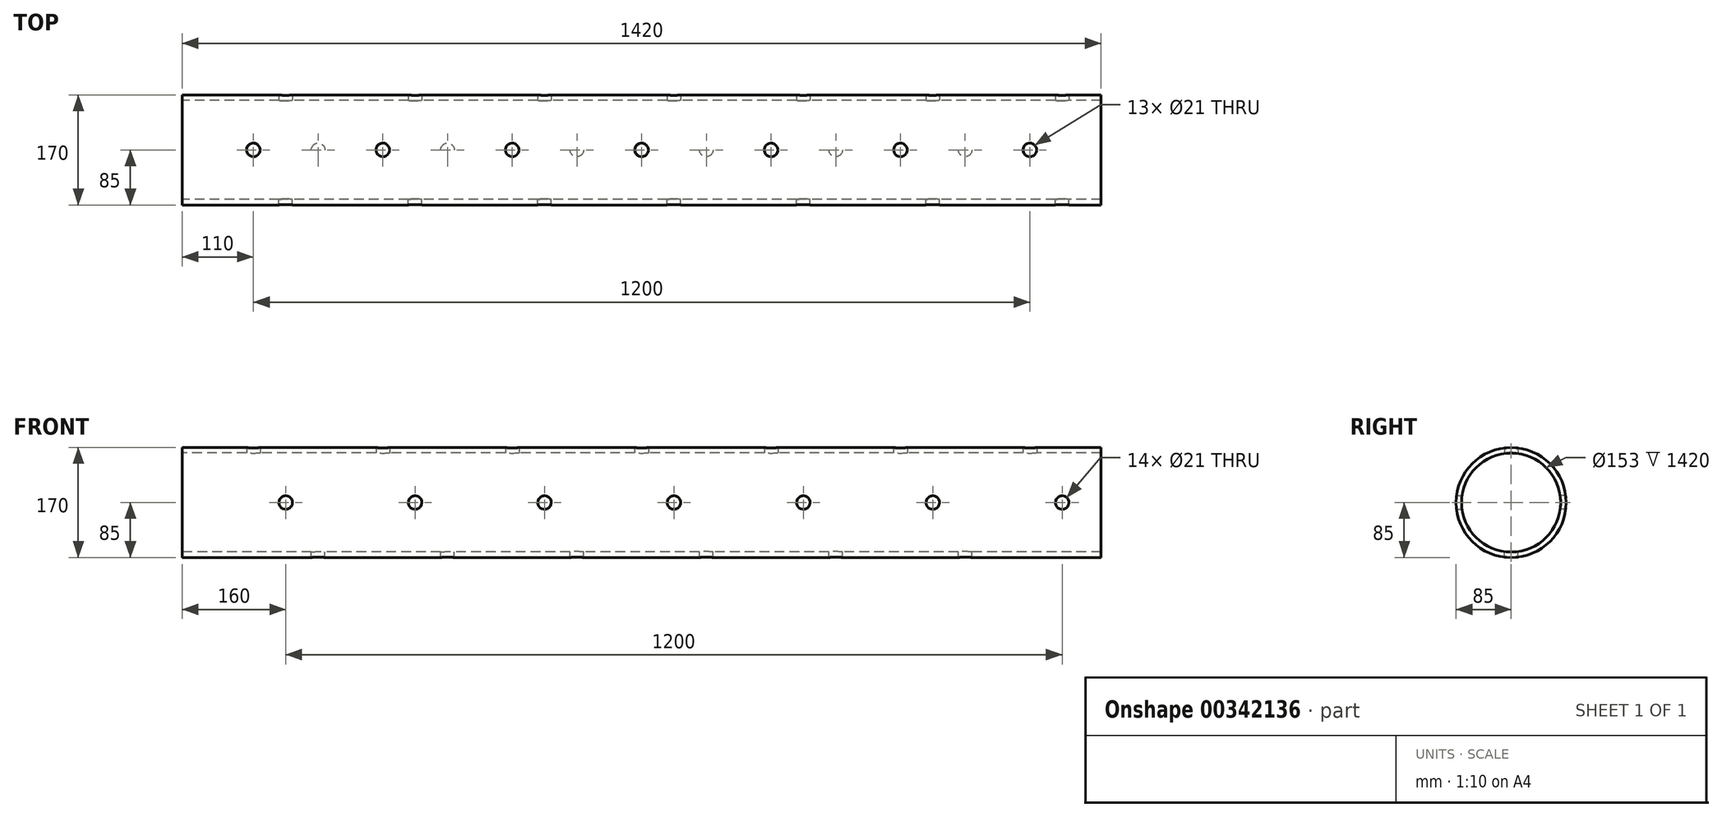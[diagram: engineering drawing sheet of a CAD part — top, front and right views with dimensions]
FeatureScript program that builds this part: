
annotation { "Feature Type Name" : "Feature", "Feature Type Description" : "" }
export const myFeature = defineFeature(function(context is Context, id is Id, definition is map)
    precondition{}
    {
        {
            var Q0;
            Q0=qCreatedBy(makeId("Right.planeOp"),FACE);
            var sketch = newSketch(context, id + "F0", { "sketchPlane" : qUnion([Q0])});
            skCircle(sketch, "E0", {"center": v(0, 0) * mm, "radius": 85 * mm});
            skCircle(sketch, "E1", {"center": v(0, 0) * mm, "radius": 76.5 * mm});
            skSolve(sketch);
        }
        {
            var Q0;
            Q0=makeQuery(id+"F0.imprint","IMPRINT",FACE,{"disambiguationData":[TD([[makeQuery(id+"F0.imprint","IMPRINT",EDGE,{"derivedFrom":sQuery(id+"F0.wireOp",EDGE,"E0")}),1.0]])]});
            extrude(context, id + "F1", {"entities" : qUnion([Q0]), "depth" : 1420 * mm});
        }
        {
            var Q0;
            Q0=qCreatedBy(makeId("Front.planeOp"),FACE);
            var sketch = newSketch(context, id + "F2", { "sketchPlane" : qUnion([Q0])});
            skLineSegment(sketch, "E2", {"start": v(0, 85) * mm, "end": v(1420, 85) * mm});
            skLineSegment(sketch, "E3", {"start": v(1420, -85) * mm, "end": v(0, -85) * mm});
            skLineSegment(sketch, "E4.0", {"start": v(0, 85) * mm, "end": v(0, -85) * mm});
            skLineSegment(sketch, "E5.0", {"start": v(1420, 85) * mm, "end": v(1420, -85) * mm});
            skLineSegment(sketch, "E6", {"start": v(0, 0) * mm, "end": v(160, 0) * mm});
            skLineSegment(sketch, "E7", {"start": v(160, 0) * mm, "end": v(360, 0) * mm});
            skLineSegment(sketch, "E8", {"start": v(360, 0) * mm, "end": v(560, 0) * mm});
            skLineSegment(sketch, "E9", {"start": v(560, 0) * mm, "end": v(760, 0) * mm});
            skLineSegment(sketch, "E10", {"start": v(760, 0) * mm, "end": v(960, 0) * mm});
            skLineSegment(sketch, "E11", {"start": v(960, 0) * mm, "end": v(1160, 0) * mm});
            skLineSegment(sketch, "E12", {"start": v(1160, 0) * mm, "end": v(1360, 0) * mm});
            skCircle(sketch, "E13", {"center": v(160, 0) * mm, "radius": 10.5 * mm});
            skCircle(sketch, "E14", {"center": v(360, 0) * mm, "radius": 10.5 * mm});
            skCircle(sketch, "E15", {"center": v(560, 0) * mm, "radius": 10.5 * mm});
            skCircle(sketch, "E16", {"center": v(760, 0) * mm, "radius": 10.5 * mm});
            skCircle(sketch, "E17", {"center": v(960, 0) * mm, "radius": 10.5 * mm});
            skCircle(sketch, "E18", {"center": v(1160, 0) * mm, "radius": 10.5 * mm});
            skCircle(sketch, "E19", {"center": v(1360, 0) * mm, "radius": 10.5 * mm});
            skSolve(sketch);
        }
        {
            var Q0;
            Q0=sQuery(id+"F2.wireOp",VERTEX,"E7.start");
            var Q1;
            Q1=sQuery(id+"F2.wireOp",VERTEX,"E8.start");
            var Q2;
            Q2=sQuery(id+"F2.wireOp",VERTEX,"E9.start");
            var Q3;
            Q3=sQuery(id+"F2.wireOp",VERTEX,"E16.center");
            var Q4;
            Q4=sQuery(id+"F2.wireOp",VERTEX,"E11.start");
            var Q5;
            Q5=sQuery(id+"F2.wireOp",VERTEX,"E12.end");
            var Q6;
            Q6=sQuery(id+"F2.wireOp",VERTEX,"E18.center");
            var Q7;
            Q7=makeQuery(id+"F1.opExtrude","SWEPT_BODY",BODY,{"disambiguationData":[OSD([sQuery(id+"F0.wireOp",EDGE,"E0"),sQuery(id+"F0.wireOp",EDGE,"E1")])]});
            hole(context, id + "F3", {"style" : HoleStyle.SIMPLE, "endStyle" : HoleEndStyle.BLIND, "holeDiameter" : 21 * mm, "holeDepth" : 1000 * mm, "tappedDepth" : 12 * mm, "tapClearance" : 3, "locations" : qUnion([Q0, Q1, Q2, Q3, Q4, Q5, Q6]), "scope" : qUnion([Q7])});
        }
        {
            var Q0;
            Q0=qCreatedBy(makeId("Front.planeOp"),FACE);
            var sketch = newSketch(context, id + "F4", { "sketchPlane" : qUnion([Q0])});
            skLineSegment(sketch, "E20.0", {"start": v(0, 85) * mm, "end": v(0, -85) * mm});
            skLineSegment(sketch, "E21", {"start": v(0, 85) * mm, "end": v(1420, 85) * mm});
            skLineSegment(sketch, "E22", {"start": v(1420, -85) * mm, "end": v(0, -85) * mm});
            skLineSegment(sketch, "E23.0", {"start": v(1420, 85) * mm, "end": v(1420, -85) * mm});
            skLineSegment(sketch, "E24", {"start": v(0, 0) * mm, "end": v(160, 0) * mm});
            skLineSegment(sketch, "E25", {"start": v(160, 0) * mm, "end": v(360, 0) * mm});
            skLineSegment(sketch, "E26", {"start": v(360, 0) * mm, "end": v(560, 0) * mm});
            skLineSegment(sketch, "E27", {"start": v(560, 0) * mm, "end": v(760, 0) * mm});
            skLineSegment(sketch, "E28", {"start": v(760, 0) * mm, "end": v(960, 0) * mm});
            skLineSegment(sketch, "E29", {"start": v(960, 0) * mm, "end": v(1160, 0) * mm});
            skLineSegment(sketch, "E30", {"start": v(1160, 0) * mm, "end": v(1360, 0) * mm});
            skSolve(sketch);
        }
        {
            var Q0;
            Q0=sQuery(id+"F4.wireOp",VERTEX,"E25.start");
            var Q1;
            Q1=sQuery(id+"F4.wireOp",VERTEX,"E26.start");
            var Q2;
            Q2=sQuery(id+"F4.wireOp",VERTEX,"E27.start");
            var Q3;
            Q3=sQuery(id+"F4.wireOp",VERTEX,"E28.start");
            var Q4;
            Q4=sQuery(id+"F4.wireOp",VERTEX,"E28.end");
            var Q5;
            Q5=sQuery(id+"F4.wireOp",VERTEX,"E29.end");
            var Q6;
            Q6=sQuery(id+"F4.wireOp",VERTEX,"E30.end");
            var Q7;
            Q7=makeQuery(id+"F1.opExtrude","SWEPT_BODY",BODY,{"disambiguationData":[OSD([sQuery(id+"F0.wireOp",EDGE,"E0"),sQuery(id+"F0.wireOp",EDGE,"E1")])]});
            hole(context, id + "F5", {"style" : HoleStyle.SIMPLE, "endStyle" : HoleEndStyle.BLIND, "oppositeDirection" : true, "holeDiameter" : 21 * mm, "holeDepth" : 1000 * mm, "tappedDepth" : 12 * mm, "tapClearance" : 3, "locations" : qUnion([Q0, Q1, Q2, Q3, Q4, Q5, Q6]), "scope" : qUnion([Q7])});
        }
        {
            var Q0;
            Q0=qCreatedBy(makeId("Top.planeOp"),FACE);
            var sketch = newSketch(context, id + "F6", { "sketchPlane" : qUnion([Q0])});
            skLineSegment(sketch, "E31", {"start": v(0, 85) * mm, "end": v(1420, 85) * mm});
            skLineSegment(sketch, "E32.0", {"start": v(0, 85) * mm, "end": v(0, -85) * mm});
            skLineSegment(sketch, "E33", {"start": v(1420, -85) * mm, "end": v(0, -85) * mm});
            skLineSegment(sketch, "E34.0", {"start": v(1420, 85) * mm, "end": v(1420, -85) * mm});
            skLineSegment(sketch, "E35", {"start": v(0, 0) * mm, "end": v(110, 0) * mm});
            skLineSegment(sketch, "E36", {"start": v(110, 0) * mm, "end": v(310, 0) * mm});
            skLineSegment(sketch, "E37", {"start": v(310, 0) * mm, "end": v(510, 0) * mm});
            skLineSegment(sketch, "E38", {"start": v(510, 0) * mm, "end": v(710, 0) * mm});
            skLineSegment(sketch, "E39", {"start": v(710, 0) * mm, "end": v(910, 0) * mm});
            skLineSegment(sketch, "E40", {"start": v(910, 0) * mm, "end": v(1110, 0) * mm});
            skLineSegment(sketch, "E41", {"start": v(1110, 0) * mm, "end": v(1310, 0) * mm});
            skLineSegment(sketch, "E42", {"start": v(0, 0) * mm, "end": v(-55.2, 0) * mm});
            skLineSegment(sketch, "E43", {"start": v(-55.2, 0) * mm, "end": v(1452.61, 0) * mm});
            skPoint(sketch, "E44", {"position": v(110, 0) * mm});
            skPoint(sketch, "E45", {"position": v(310, 0) * mm});
            skPoint(sketch, "E46", {"position": v(510, 0) * mm});
            skPoint(sketch, "E47", {"position": v(710, 0) * mm});
            skPoint(sketch, "E48", {"position": v(910, 0) * mm});
            skPoint(sketch, "E49", {"position": v(1110, 0) * mm});
            skPoint(sketch, "E50", {"position": v(1310, 0) * mm});
            skSolve(sketch);
        }
        {
            var Q0;
            Q0=sQuery(id+"F6.wireOp",VERTEX,"E46");
            var Q1;
            Q1=sQuery(id+"F6.wireOp",VERTEX,"E45");
            var Q2;
            Q2=sQuery(id+"F6.wireOp",VERTEX,"E44");
            var Q3;
            Q3=sQuery(id+"F6.wireOp",VERTEX,"E48");
            var Q4;
            Q4=sQuery(id+"F6.wireOp",VERTEX,"E47");
            var Q5;
            Q5=sQuery(id+"F6.wireOp",VERTEX,"E49");
            var Q6;
            Q6=sQuery(id+"F6.wireOp",VERTEX,"E50");
            var Q7;
            Q7=makeQuery(id+"F1.opExtrude","SWEPT_BODY",BODY,{"disambiguationData":[OSD([sQuery(id+"F0.wireOp",EDGE,"E0"),sQuery(id+"F0.wireOp",EDGE,"E1")])]});
            hole(context, id + "F7", {"style" : HoleStyle.SIMPLE, "endStyle" : HoleEndStyle.BLIND, "oppositeDirection" : true, "holeDiameter" : 21 * mm, "holeDepth" : 100 * mm, "tappedDepth" : 12 * mm, "tapClearance" : 3, "locations" : qUnion([Q0, Q1, Q2, Q3, Q4, Q5, Q6]), "scope" : qUnion([Q7])});
        }
        {
            var Q0;
            Q0=qCreatedBy(makeId("Top.planeOp"),FACE);
            var sketch = newSketch(context, id + "F8", { "sketchPlane" : qUnion([Q0])});
            skLineSegment(sketch, "E51", {"start": v(0, 0) * mm, "end": v(210, 0) * mm});
            skLineSegment(sketch, "E52", {"start": v(210, 0) * mm, "end": v(410, 0) * mm});
            skLineSegment(sketch, "E53", {"start": v(410, 0) * mm, "end": v(610, 0) * mm});
            skLineSegment(sketch, "E54", {"start": v(610, 0) * mm, "end": v(810, 0) * mm});
            skLineSegment(sketch, "E55", {"start": v(810, 0) * mm, "end": v(1010, 0) * mm});
            skLineSegment(sketch, "E56", {"start": v(1010, 0) * mm, "end": v(1210, 0) * mm});
            skSolve(sketch);
        }
        {
            var Q0;
            Q0=sQuery(id+"F8.wireOp",VERTEX,"E51.end");
            var Q1;
            Q1=sQuery(id+"F8.wireOp",VERTEX,"E52.end");
            var Q2;
            Q2=sQuery(id+"F8.wireOp",VERTEX,"E53.end");
            var Q3;
            Q3=sQuery(id+"F8.wireOp",VERTEX,"E54.end");
            var Q4;
            Q4=sQuery(id+"F8.wireOp",VERTEX,"E55.end");
            var Q5;
            Q5=sQuery(id+"F8.wireOp",VERTEX,"E56.end");
            var Q6;
            Q6=makeQuery(id+"F1.opExtrude","SWEPT_BODY",BODY,{"disambiguationData":[OSD([sQuery(id+"F0.wireOp",EDGE,"E0"),sQuery(id+"F0.wireOp",EDGE,"E1")])]});
            hole(context, id + "F9", {"style" : HoleStyle.SIMPLE, "endStyle" : HoleEndStyle.BLIND, "holeDiameter" : 21 * mm, "holeDepth" : 100 * mm, "tappedDepth" : 12 * mm, "tapClearance" : 3, "locations" : qUnion([Q0, Q1, Q2, Q3, Q4, Q5]), "scope" : qUnion([Q6])});
        }
    });
